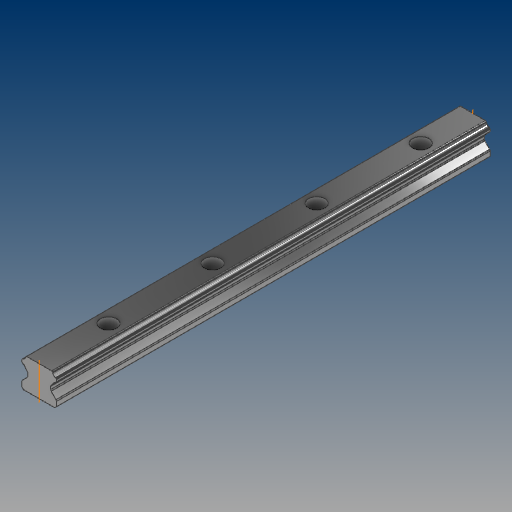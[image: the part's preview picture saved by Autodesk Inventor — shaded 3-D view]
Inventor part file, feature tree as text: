
AUTODESK INVENTOR PART (.ipt)
format: ipt  version: 2021 (Build 250183000, 183)  size: 314,880 bytes
history: native  units: mm
features: sketch x4, extrude x3, projected_geometry x3, other x2
ambient origin geometry x8: Origin, YZ Plane, XZ Plane, XY Plane, X Axis, Y Axis, Z Axis, Center Point
bodies: Solid1 (feature_tree)
feature tree (12):
  extrude  "Extrusion1"  Depth=250.0mm
  sketch  "Sketch2"  dims[d4=6.0mm d6=9.5mm d7=6.0mm]
  extrude  "Extrusion2"  Depth=9.5mm
  extrude  "Extrusion3"  Depth=9.5mm
  sketch  "Sketch3"  dims[d9=9.5mm d10=6.0mm d12=9.5mm d13=6.0mm]
  other  "Work Axis1"
  sketch  "Sketch4"  dims[d15=9.5mm d16=6.0mm d18=9.5mm d19=6.0mm d21=9.5mm d22=6.0mm d24=9.5mm d25=6.0mm d27=9.5mm d28=6.0mm d30=9.5mm d31=6.0mm d33=9.5mm d34=6.0mm d36=9.5mm d37=6.0mm d39=9.5mm d40=6.0mm d42=9.5mm d43=6.0mm d45=9.5mm d46=6.0mm d48=9.5mm d49=6.0mm d51=9.5mm d52=6.0mm d54=9.5mm d55=6.0mm d57=9.5mm d58=6.0mm d60=9.5mm d61=6.0mm d63=9.5mm d64=6.0mm d66=9.5mm d67=6.0mm d69=9.5mm d70=6.0mm d72=9.5mm d73=6.0mm d75=9.5mm d76=6.0mm d78=30.0mm d79=0.0mm d80=8.4mm d81=0.0mm d82=18.0mm d83=14.471441mm]
  other  "Work Axis2"
  sketch  "Sketch1"  dims[d0=250.0mm d1=0.0mm d3=9.5mm]
  projected_geometry  "Projected Loop1"
  projected_geometry  "Projected Loop2"
  projected_geometry  "Projected Loop3"
